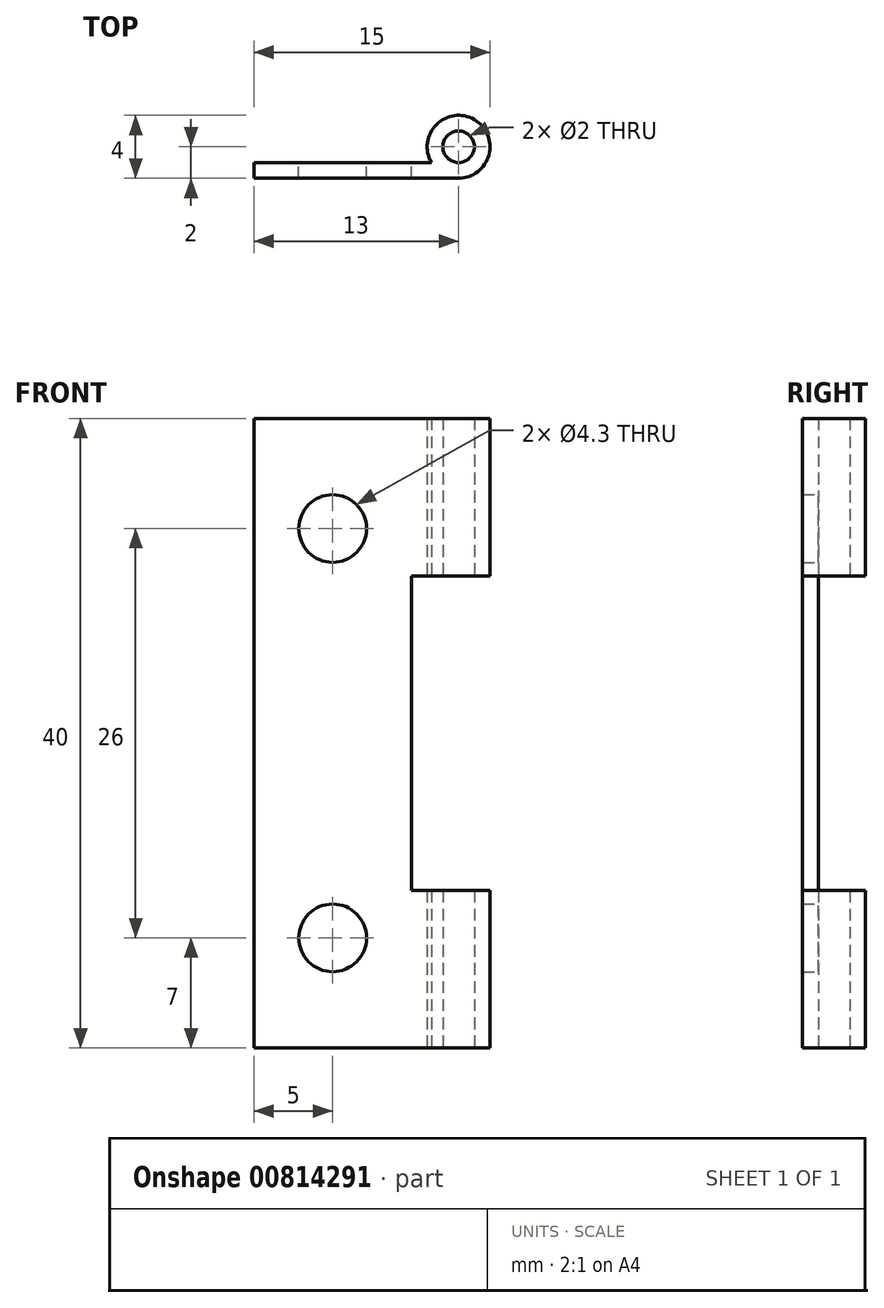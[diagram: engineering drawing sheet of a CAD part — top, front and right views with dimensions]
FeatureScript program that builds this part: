
annotation { "Feature Type Name" : "Feature", "Feature Type Description" : "" }
export const myFeature = defineFeature(function(context is Context, id is Id, definition is map)
    precondition{}
    {
        {
            var Q0;
            Q0=qCreatedBy(makeId("Front.planeOp"),FACE);
            var sketch = newSketch(context, id + "F0", { "sketchPlane" : qUnion([Q0])});
            skLineSegment(sketch, "E0.bottom", {"start": v(5, 20) * mm, "end": v(-5, 20) * mm});
            skLineSegment(sketch, "E0.top", {"start": v(5, -20) * mm, "end": v(-5, -20) * mm});
            skLineSegment(sketch, "E0.left", {"start": v(5, 20) * mm, "end": v(5, -20) * mm});
            skLineSegment(sketch, "E0.right", {"start": v(-5, 20) * mm, "end": v(-5, -20) * mm});
            skPoint(sketch, "E0.middle", {"position": v(0, 0) * mm});
            skLineSegment(sketch, "E1.left", {"start": v(5, 20) * mm, "end": v(5, 10) * mm});
            skLineSegment(sketch, "E2.left", {"start": v(5, -20) * mm, "end": v(5, -10) * mm});
            skLineSegment(sketch, "E3.bottom", {"start": v(5, 20) * mm, "end": v(8, 20) * mm});
            skLineSegment(sketch, "E3.top", {"start": v(5, 10) * mm, "end": v(8, 10) * mm});
            skLineSegment(sketch, "E3.right", {"start": v(8, 20) * mm, "end": v(8, 10) * mm});
            skLineSegment(sketch, "E4.bottom", {"start": v(5, -10) * mm, "end": v(8, -10) * mm});
            skLineSegment(sketch, "E4.top", {"start": v(5, -20) * mm, "end": v(8, -20) * mm});
            skLineSegment(sketch, "E4.left", {"start": v(5, -10) * mm, "end": v(5, -20) * mm});
            skLineSegment(sketch, "E4.right", {"start": v(8, -10) * mm, "end": v(8, -20) * mm});
            skSolve(sketch);
        }
        {
            var Q0;
            Q0=makeQuery(id+"F0.imprint","IMPRINT",FACE,{"disambiguationData":[TD([[makeQuery(id+"F0.imprint","IMPRINT",EDGE,{"derivedFrom":sQuery(id+"F0.wireOp",EDGE,"E0.bottom")}),1.0]])]});
            var Q1;
            Q1=makeQuery(id+"F0.imprint","IMPRINT",FACE,{"disambiguationData":[TD([[makeQuery(id+"F0.imprint","IMPRINT",EDGE,{"derivedFrom":sQuery(id+"F0.wireOp",EDGE,"E4.bottom")}),-1.0]])]});
            var Q2;
            Q2=makeQuery(id+"F0.imprint","IMPRINT",FACE,{"disambiguationData":[TD([[makeQuery(id+"F0.imprint","IMPRINT",EDGE,{"derivedFrom":sQuery(id+"F0.wireOp",EDGE,"E3.bottom")}),-1.0]])]});
            extrude(context, id + "F1", {"entities" : qUnion([Q0, Q1, Q2]), "depth" : 1 * mm, "offsetDistance" : 25 * mm});
        }
        {
            var Q0;
            Q0=makeQuery(id+"F1.opExtrude","SWEPT_FACE",FACE,{"disambiguationData":[OSD([sQuery(id+"F0.wireOp",EDGE,"E4.right")])]});
            var sketch = newSketch(context, id + "F2", { "sketchPlane" : qUnion([Q0])});
            skLineSegment(sketch, "E5.0.0", {"start": v(0, 10) * mm, "end": v(0, 20) * mm});
            skLineSegment(sketch, "E5.0.1", {"start": v(0, 20) * mm, "end": v(-1, 20) * mm});
            skLineSegment(sketch, "E5.0.2", {"start": v(-1, 20) * mm, "end": v(-1, 10) * mm});
            skLineSegment(sketch, "E5.0.3", {"start": v(-1, 10) * mm, "end": v(0, 10) * mm});
            skLineSegment(sketch, "E6", {"start": v(1, -20) * mm, "end": v(1, 20) * mm, "construction": true});
            skSolve(sketch);
        }
        {
            var Q0;
            {var subQ0=sQuery(id+"F0.wireOp",EDGE,"E4.right");Q0=makeQuery(id+"F2.imprint","IMPRINT",FACE,{"disambiguationData":[TD([[makeQuery(id+"F2.imprint","IMPRINT",EDGE,{"derivedFrom":makeQuery(id+"F1.opExtrude","CAP_EDGE",EDGE,{"disambiguationData":[OSD([subQ0])],"isStart":true})}),-1.0]])]});}
            var Q1;
            Q1=makeQuery(id+"F2.imprint","IMPRINT",FACE,{"disambiguationData":[TD([[makeQuery(id+"F2.imprint","IMPRINT",EDGE,{"derivedFrom":sQuery(id+"F2.wireOp",EDGE,"E5.0.0")}),1.0]])]});
            var Q2;
            Q2=sQuery(id+"F2.wireOp",EDGE,"E6");
            revolve(context, id + "F3", {"operationType" : NewBodyOperationType.ADD, "surfaceOperationType" : NewSurfaceOperationType.NEW, "entities" : qUnion([Q0, Q1]), "axis" : qUnion([Q2]), "revolveType" : RevolveType.FULL});
        }
        {
            var Q0;
            Q0=makeQuery(id+"F1.opExtrude","CAP_FACE",FACE,{"disambiguationData":[OSD([sQuery(id+"F0.wireOp",EDGE,"E0.bottom"),sQuery(id+"F0.wireOp",EDGE,"E0.top"),sQuery(id+"F0.wireOp",EDGE,"E0.left"),sQuery(id+"F0.wireOp",EDGE,"E0.right"),sQuery(id+"F0.wireOp",EDGE,"E3.bottom"),sQuery(id+"F0.wireOp",EDGE,"E3.top"),sQuery(id+"F0.wireOp",EDGE,"E3.right"),sQuery(id+"F0.wireOp",EDGE,"E4.bottom"),sQuery(id+"F0.wireOp",EDGE,"E4.top"),sQuery(id+"F0.wireOp",EDGE,"E4.right")])],"isStart":false});
            var sketch = newSketch(context, id + "F4", { "sketchPlane" : qUnion([Q0])});
            skPoint(sketch, "E7", {"position": v(0, -13) * mm});
            skPoint(sketch, "E8", {"position": v(0, 13) * mm});
            skSolve(sketch);
        }
        {
            var Q0;
            Q0=sQuery(id+"F4.wireOp",VERTEX,"E8");
            var Q1;
            Q1=sQuery(id+"F4.wireOp",VERTEX,"E7");
            var Q2;
            Q2=makeQuery(id+"F1.opExtrude","SWEPT_BODY",BODY,{"disambiguationData":[OSD([sQuery(id+"F0.wireOp",EDGE,"E0.bottom"),sQuery(id+"F0.wireOp",EDGE,"E0.top"),sQuery(id+"F0.wireOp",EDGE,"E0.left"),sQuery(id+"F0.wireOp",EDGE,"E0.right"),sQuery(id+"F0.wireOp",EDGE,"E3.bottom"),sQuery(id+"F0.wireOp",EDGE,"E3.top"),sQuery(id+"F0.wireOp",EDGE,"E3.right"),sQuery(id+"F0.wireOp",EDGE,"E4.bottom"),sQuery(id+"F0.wireOp",EDGE,"E4.top"),sQuery(id+"F0.wireOp",EDGE,"E4.right")])]});
            hole(context, id + "F5", {"style" : HoleStyle.SIMPLE, "endStyle" : HoleEndStyle.BLIND, "holeDiameter" : 4.3 * mm, "majorDiameter" : 5 * mm, "holeDepth" : 2.5 * mm, "isTappedThrough" : true, "tappedDepth" : 12 * mm, "tapClearance" : 3, "locations" : qUnion([Q0, Q1]), "scope" : qUnion([Q2]), "startStyle" : HoleStartStyle.SKETCH});
        }
    });
